# Revit family: Storage-Teknion-CMPD_Mobile_Pedestal-R2021
name_source: partatom
category: Furniture
units: mm (PartAtom-declared; Revit-internal decimal feet)

## family parameters
Always vertical = Yes
Cut with Voids When Loaded = No
OmniClass Number = 23.40.20.00
OmniClass Title = General Furniture and Specialties
Room Calculation Point = No
Shared = Yes
Work Plane-Based = No

## types (4) — shared parameters
Assembly Code = E2020200
Manufacturer = Teknion
Manufacturer Fax = 416.661.4586
Part Number = CMPD
Product Documentation Link = https://www.teknion.com
Product Line = Chronicle
Product Page URL = https://www.teknion.com
Series = Chronicle
Sustainability Data = https://www.teknion.com
URL = www.teknion.com
Unit Weight URL = http://www.teknion.com
Warranty = http://www.teknion.com
zero-valued in all types: Default Elevation

## per-type parameters (varying)
| type | Case - Front - Bottom | Case - Front - Top & Bottom - Front Gap | Case - Side - Front Gap | Caster - Front | Cut-Out - Front | Description | Front | Left/Right Handed Hinged Door | Model | Open | Shelf | Shelf - Front Gap | Top - Inset - Front Gap |
| Open | Yes | 0 " | 0 " | 6.085 " | 0.5 " | Mobile Pedestal, Open Storage, 20" Depth, 15" Width | No | No | CMPDO__2015 | Yes | Yes | 1 " | 0.724 " |
| 1 Box, 1 File | No | 0.843 " | 0.843 " | 5.242 " | 2 " | Mobile Pedestal, 1 Box, 1 File Storage, 20" Depth, 15" Width | Yes | No | CMPDX__2015_ | No | No | 1.843 " | 1.567 " |
| Left Handed Hinged Door | Yes | 0.843 " | 0.843 " | 5.242 " | 0.5 " | Mobile Pedestal, Left Handed Hinged Door Storage, 20" Depth, 15" Width | Yes | Yes | CMPDL__2015_ | No | Yes | 1.843 " | 1.567 " |
| Right Handed Hinged Door | Yes | 0.843 " | 0.843 " | 5.242 " | 0.5 " | Mobile Pedestal, Right Handed Hinged Door Storage, 20" Depth, 15" Width | Yes | Yes | CMPDR__2015_ | No | Yes | 1.843 " | 1.567 " |

type visibility flags (boolean, named after types; folded from table):
- Open: Yes: (none)
- 1 Box, 1 File: Yes: 1 Box, 1 File
- Left Handed Hinged Door: Yes: (none)
- Right Handed Hinged Door: Yes: (none)

## geometry (parser evidence)
native form markers: Sweep x3
no freeform markers — native parametric forms only
